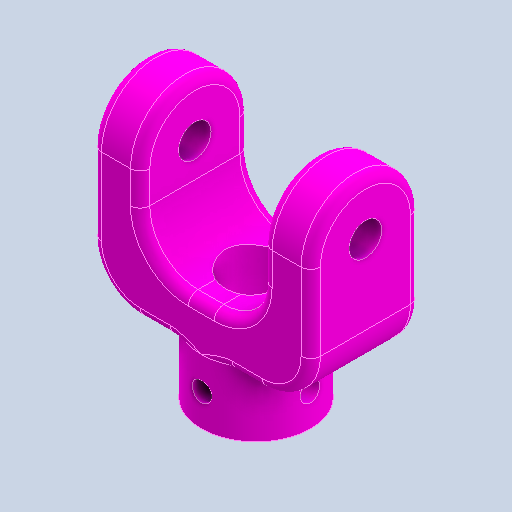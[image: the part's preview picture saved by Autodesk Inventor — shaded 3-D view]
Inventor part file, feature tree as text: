
AUTODESK INVENTOR PART (.ipt)
format: ipt  version: 2022 (Build 260153000, 153)  size: 306,688 bytes
history: native  units: in
note: dims shown in document units (in); Inventor stores cm internally (conversion verified against a paired STEP export)
features: sketch x5, other x4, plane x1
ambient origin geometry x8: Origin, YZ Plane, XZ Plane, XY Plane, X Axis, Y Axis, Z Axis, Center Point
bodies: Solid1 (feature_tree)
feature tree (10):
  other  "fork.ipt"
  other  "Solid1::fork.ipt"
  other  "TaggingFeature1"
  sketch  "Sketch1"  dims[d0=0.3937in]
  sketch  "Sketch2"
  sketch  "Sketch3"
  sketch  "Sketch4"
  sketch  "Sketch5"
  plane  "Work Plane1"
  other  "Work Axis1"
